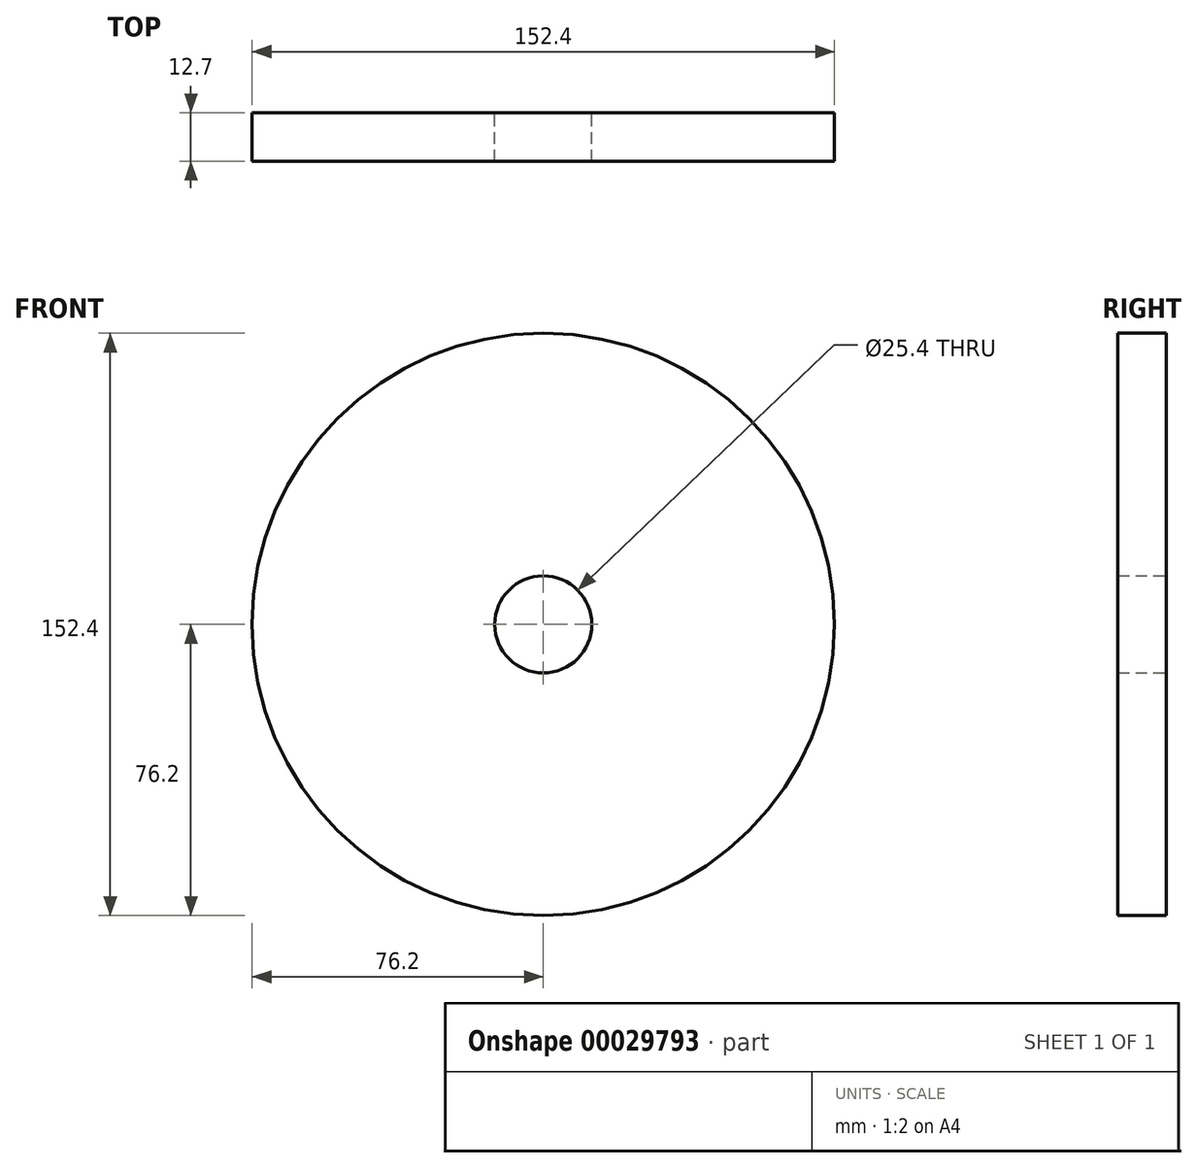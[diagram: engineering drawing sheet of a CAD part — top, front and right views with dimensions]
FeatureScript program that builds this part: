
annotation { "Feature Type Name" : "Feature", "Feature Type Description" : "" }
export const myFeature = defineFeature(function(context is Context, id is Id, definition is map)
    precondition{}
    {
        {
            var Q0;
            Q0=qCreatedBy(makeId("Front.planeOp"),FACE);
            var sketch = newSketch(context, id + "F0", { "sketchPlane" : qUnion([Q0])});
            skCircle(sketch, "E0", {"center": v(0, 0) * mm, "radius": 76.2 * mm});
            skLineSegment(sketch, "E1", {"start": v(0, 0) * mm, "end": v(0, 76.2) * mm});
            skCircle(sketch, "E2", {"center": v(0, 0) * mm, "radius": 12.7 * mm});
            skLineSegment(sketch, "E3", {"start": v(0, 0) * mm, "end": v(0, -12.7) * mm});
            skSolve(sketch);
        }
        {
            var Q0;
            Q0=makeQuery(id+"F0.imprint","IMPRINT",FACE,{"disambiguationData":[TD([[makeQuery(id+"F0.imprint","IMPRINT",EDGE,{"derivedFrom":sQuery(id+"F0.wireOp",EDGE,"E0")}),1.0]])]});
            extrude(context, id + "F1", {"entities" : qUnion([Q0]), "depth" : 12.7 * mm});
        }
    });
